# Revit family: Sink-Vessel-Lavatory-KOHLER-CONICAL_BELL-K-2200T
name_source: partatom
category: Plumbing Fixtures
revit_build: Autodesk Revit 2017 (Build: 20160225_1515(x64)
units: mm (PartAtom-declared; Revit-internal decimal feet)

## family parameters
Cut with Voids When Loaded = No
Host = Face
OmniClass Number = 23.31.13.00
OmniClass Title = Sinks
Part Type = Normal
Room Calculation Point = No
Round Connector Dimension = Use Diameter
Shared = No

## types (5) — shared parameters
ADA Compliant = No
Assembly Code = D2010400
CW Connection = No
Cold Water Inlet = Cold Water Inlet
Date Modified = 07/02/2020
Default Elevation = 36"
Description = Vessels Conical Bell Lavatory with Glazed Bottom
Drain Included = No
HW Connection = No
Height = 6 3/8"
Hot Water Inlet = Hot Water Inlet
Length = 16 1/4"
Manufacturer = KOHLER Co.
Master Format 2014 = 22 41 16
Master Format 2014 Name = Residential Lavatories and Sinks
Material = Vitrous China
Product Name = CONICAL BELL
URL = http://www.kohler.com.cn
Vent Connection = No
Waste Connection = Yes
Waste Water Outlet = Waste Water Outlet
WaterSense Certified = No
Width = 16 1/4"

## per-type parameters (varying)
| type | Finish | Model | Type |
| 0-White | Kohler-Vitreous_China-0-White | K-2200T-G-0 | 1 |
| 47-Almond | Kohler-Vitreous_China-47-Almond | K-2200T-G-47 | 2 |
| 71-Seafoam | KOHLER-Vitreous_China-71-Seafoam | K-2200T-G-71 | 3 |
| 95-Ice Grey | Kohler-Vitreous_China-95-Ice_Grey | K-2200T-G-95 | 4 |
| 96-Biscuit | Kohler-Vitreous_China-96-Biscuit | K-2200T-G-96 | 5 |

## geometry (parser evidence)
native form markers: Sweep x4
no freeform markers — native parametric forms only
